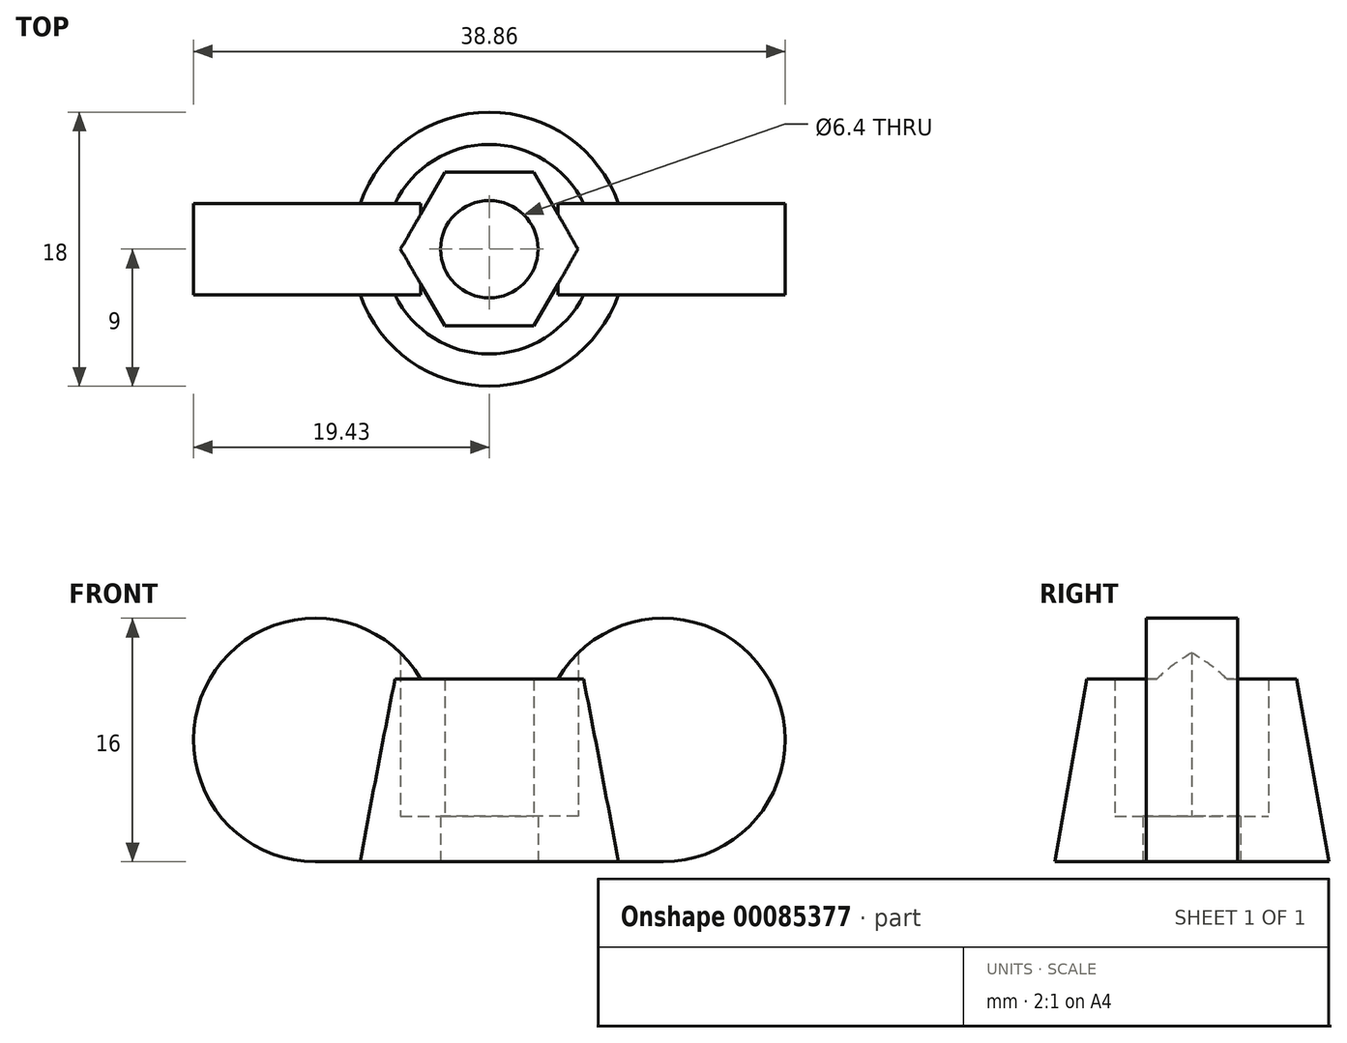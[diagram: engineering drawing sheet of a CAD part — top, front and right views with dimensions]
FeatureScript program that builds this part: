
annotation { "Feature Type Name" : "Feature", "Feature Type Description" : "" }
export const myFeature = defineFeature(function(context is Context, id is Id, definition is map)
    precondition{}
    {
        {
            var Q0;
            Q0=qCreatedBy(makeId("Top.planeOp"),FACE);
            var sketch = newSketch(context, id + "F0", { "sketchPlane" : qUnion([Q0])});
            skCircle(sketch, "E0", {"center": v(0, 0) * mm, "radius": 9 * mm});
            skCircle(sketch, "E1", {"center": v(0, 0) * mm, "radius": 3.2 * mm});
            skCircle(sketch, "E2.cCircle", {"center": v(0, 0) * mm, "radius": 5.05 * mm, "construction": true});
            skLineSegment(sketch, "E2.0", {"start": v(-2.92, 5.05) * mm, "end": v(2.92, 5.05) * mm});
            skLineSegment(sketch, "E2.1", {"start": v(2.92, 5.05) * mm, "end": v(5.83, 0) * mm});
            skLineSegment(sketch, "E2.2", {"start": v(5.83, 0) * mm, "end": v(2.92, -5.05) * mm});
            skLineSegment(sketch, "E2.3", {"start": v(2.92, -5.05) * mm, "end": v(-2.92, -5.05) * mm});
            skLineSegment(sketch, "E2.4", {"start": v(-2.92, -5.05) * mm, "end": v(-5.83, 0) * mm});
            skLineSegment(sketch, "E2.5", {"start": v(-5.83, 0) * mm, "end": v(-2.92, 5.05) * mm});
            skPoint(sketch, "E2.0.midPoint", {"position": v(0, 5.05) * mm});
            skSolve(sketch);
        }
        {
            var Q0;
            Q0=makeQuery(id+"F0.imprint","IMPRINT",FACE,{"disambiguationData":[TD([[makeQuery(id+"F0.imprint","IMPRINT",EDGE,{"derivedFrom":sQuery(id+"F0.wireOp",EDGE,"E0")}),1.0]])]});
            var Q1;
            Q1=makeQuery(id+"F0.imprint","IMPRINT",FACE,{"disambiguationData":[TD([[makeQuery(id+"F0.imprint","IMPRINT",EDGE,{"derivedFrom":sQuery(id+"F0.wireOp",EDGE,"E1")}),-1.0]])]});
            var Q2;
            Q2=makeQuery(id+"F0.imprint","IMPRINT",FACE,{"disambiguationData":[TD([[makeQuery(id+"F0.imprint","IMPRINT",EDGE,{"derivedFrom":sQuery(id+"F0.wireOp",EDGE,"E1")}),1.0]])]});
            extrude(context, id + "F1", {"entities" : qUnion([Q0, Q1, Q2]), "depth" : 12 * mm, "hasDraft" : true, "draftAngle" : 10 * degree, "draftPullDirection" : true});
        }
        {
            var Q0;
            Q0=qCreatedBy(makeId("Front.planeOp"),FACE);
            var sketch = newSketch(context, id + "F2", { "sketchPlane" : qUnion([Q0])});
            skLineSegment(sketch, "E3.0", {"start": v(-6.88, 12) * mm, "end": v(6.88, 12) * mm});
            skLineSegment(sketch, "E3.1", {"start": v(-11.43, 0) * mm, "end": v(11.43, 0) * mm});
            skArc(sketch, "E4", {"start": v(11.43, 0) * mm, "mid": v(18.36, 12) * mm, "end": v(4.5, 12) * mm});
            skPoint(sketch, "E5.orphan", {"position": v(9, 0) * mm});
            skLineSegment(sketch, "E6", {"start": v(0, 0) * mm, "end": v(0, -3.25) * mm});
            skArc(sketch, "E7.MirrorCS", {"start": v(-11.43, 0) * mm, "mid": v(-18.36, 12) * mm, "end": v(-4.5, 12) * mm});
            skPoint(sketch, "E8.orphan", {"position": v(-9, 0) * mm});
            skSolve(sketch);
        }
        {
            var Q0;
            Q0 = qSketchRegion(id + "F2", true);
            extrude(context, id + "F3", {"entities" : qUnion([Q0]), "operationType" : NewBodyOperationType.ADD, "depth" : 6 * mm, "symmetric" : true});
        }
        {
            var Q0;
            Q0=makeQuery(id+"F0.imprint","IMPRINT",FACE,{"disambiguationData":[TD([[makeQuery(id+"F0.imprint","IMPRINT",EDGE,{"derivedFrom":sQuery(id+"F0.wireOp",EDGE,"E1")}),1.0]])]});
            var Q1;
            Q1=makeQuery(id+"F1.opExtrude","CAP_FACE",FACE,{"disambiguationData":[OSD([sQuery(id+"F0.wireOp",EDGE,"E0")])],"isStart":false});
            extrude(context, id + "F4", {"entities" : qUnion([Q0]), "operationType" : NewBodyOperationType.REMOVE, "endBound" : BoundingType.UP_TO_SURFACE, "endBoundEntityFace" : qUnion([Q1]), "depth" : 25 * mm});
        }
        {
            var Q0;
            Q0=makeQuery(id+"F0.imprint","IMPRINT",FACE,{"disambiguationData":[TD([[makeQuery(id+"F0.imprint","IMPRINT",EDGE,{"derivedFrom":sQuery(id+"F0.wireOp",EDGE,"E1")}),-1.0]])]});
            extrude(context, id + "F5", {"entities" : qUnion([Q0]), "operationType" : NewBodyOperationType.REMOVE, "depth" : 25 * mm, "hasSecondDirection" : true, "secondDirectionOppositeDirection" : false, "secondDirectionDepth" : 3 * mm});
        }
    });
